# Revit family: 13284 Столик «Eco lounge» Хоббика
name_source: partatom
category: Антураж
revit_build: Autodesk Revit 2018 (Build: 20180423_1000(x64)
units: mm (PartAtom-declared; Revit-internal decimal feet)

## family parameters
Всегда вертикально = Да
Источник визуального образа = Геометрия семейства
На основе рабочей плоскости = Нет
Общий = Нет
При загрузке вырезать с полостями = Нет
Точка расчета площади = Нет

## types (2) — shared parameters
URL = https://hobbyka.ru
Артикул товара = Арт. 13284
Высота = 300 мм
Группа модели = Мебель для дома и террас
Длина = 750 мм
Изготовитель = ООО «Хоббика»
Изображение типоразмера = Столик «Eco lounge» Арт 13284.jpg
Материал изделия = Дерево
Цвет отделки = Ангарская сосна
Ширина = 750 мм

## per-type parameters (varying)
| type | Версия ангарская сосна | Версия лиственница | Описание |
| Версия ангарская сосна | Да | Нет | Столик «Eco lounge». Версия ангарская сосна |
| Версия лиственница | Нет | Да | Столик «Eco lounge». Версия лиственница |
